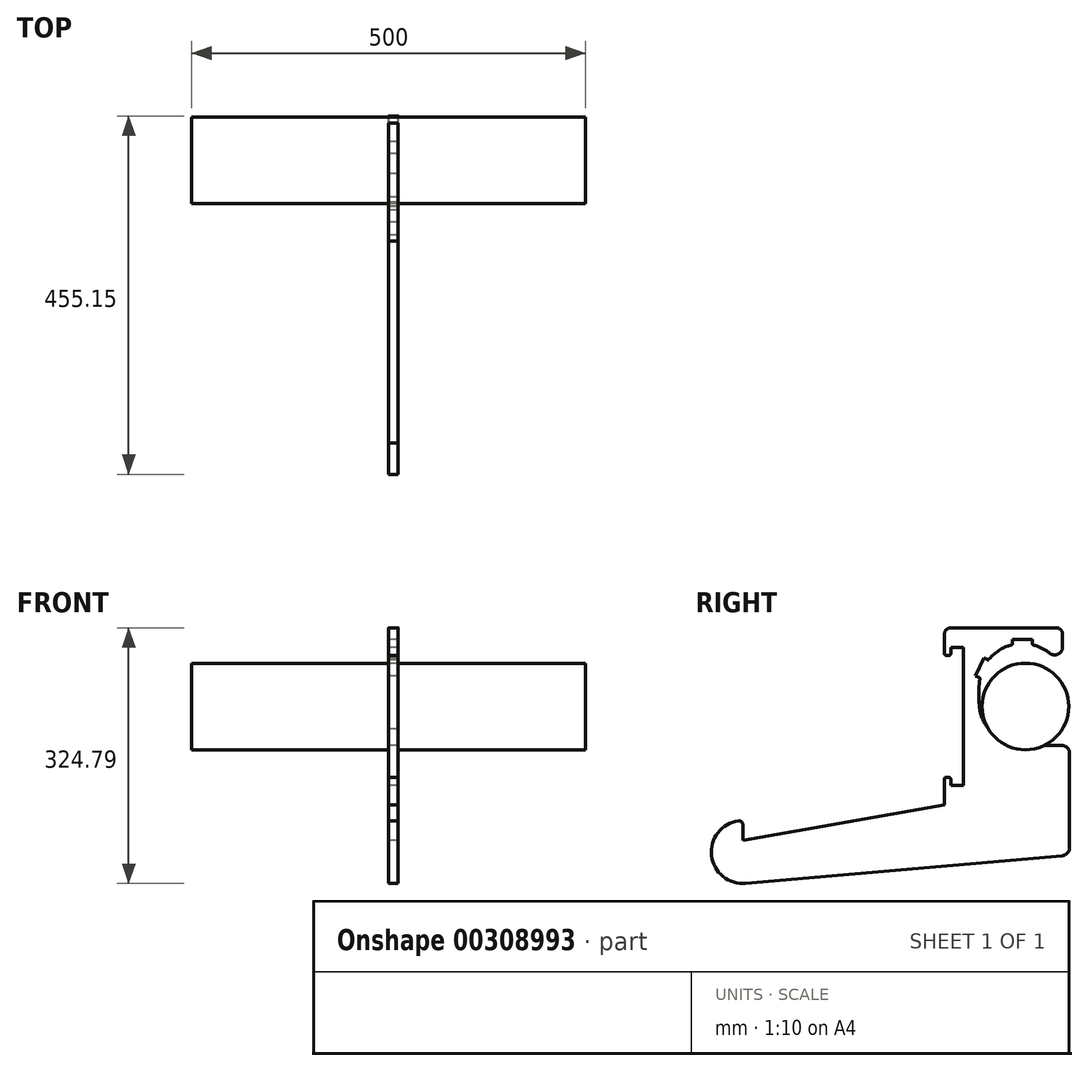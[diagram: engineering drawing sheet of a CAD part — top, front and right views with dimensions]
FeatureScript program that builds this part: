
annotation { "Feature Type Name" : "Feature", "Feature Type Description" : "" }
export const myFeature = defineFeature(function(context is Context, id is Id, definition is map)
    precondition{}
    {
        {
            var Q0;
            Q0=qCreatedBy(makeId("Right.planeOp"),FACE);
            var sketch = newSketch(context, id + "F0", { "sketchPlane" : qUnion([Q0])});
            skCircle(sketch, "E0", {"center": v(-60, 100) * mm, "radius": 55 * mm});
            skSolve(sketch);
        }
        {
            var Q0;
            Q0=makeQuery(id+"F0.imprint","IMPRINT",FACE,{"disambiguationData":[TD([[makeQuery(id+"F0.imprint","IMPRINT",EDGE,{"derivedFrom":sQuery(id+"F0.wireOp",EDGE,"E0")}),1.0]])]});
            extrude(context, id + "F1", {"entities" : qUnion([Q0]), "depth" : 250 * mm, "hasSecondDirection" : true, "secondDirectionOppositeDirection" : true, "secondDirectionDepth" : 250 * mm});
        }
        {
            var Q0;
            Q0=qCreatedBy(makeId("Right.planeOp"),FACE);
            var sketch = newSketch(context, id + "F2", { "sketchPlane" : qUnion([Q0])});
            skLineSegment(sketch, "E1", {"start": v(-12.91, 175.52) * mm, "end": v(-12.91, 200) * mm});
            skLineSegment(sketch, "E2", {"start": v(-12.91, 200) * mm, "end": v(-162.91, 200) * mm});
            skLineSegment(sketch, "E3", {"start": v(-162.91, 200) * mm, "end": v(-162.91, 165) * mm});
            skLineSegment(sketch, "E4", {"start": v(-162.91, -25) * mm, "end": v(-418.96, -70.15) * mm});
            skLineSegment(sketch, "E5", {"start": v(-118.81, 105.52) * mm, "end": v(-118.81, 125) * mm});
            skArc(sketch, "E6", {"start": v(-29.2, 167.75) * mm, "mid": v(-39.65, 174.4) * mm, "end": v(-51.31, 178.56) * mm});
            skLineSegment(sketch, "E7.top", {"start": v(-76.31, 185) * mm, "end": v(-51.31, 185) * mm});
            skLineSegment(sketch, "E7.left", {"start": v(-76.31, 178.56) * mm, "end": v(-76.31, 185) * mm});
            skLineSegment(sketch, "E7.right", {"start": v(-51.31, 178.56) * mm, "end": v(-51.31, 185) * mm});
            skLineSegment(sketch, "E8", {"start": v(-107.07, 158.96) * mm, "end": v(-112.9, 161.69) * mm});
            skLineSegment(sketch, "E9", {"start": v(-112.9, 161.69) * mm, "end": v(-123.47, 139.03) * mm});
            skLineSegment(sketch, "E10", {"start": v(-123.47, 139.03) * mm, "end": v(-117.64, 136.3) * mm});
            skPoint(sketch, "E11", {"position": v(-63.81, 185) * mm});
            skArc(sketch, "E12.trimOffspring", {"start": v(-76.31, 178.56) * mm, "mid": v(-93.36, 171.39) * mm, "end": v(-107.07, 158.96) * mm});
            skLineSegment(sketch, "E13", {"start": v(-63.81, 125) * mm, "end": v(-118.2, 150.36) * mm, "construction": true});
            skArc(sketch, "E14.trimOffspring", {"start": v(-117.64, 136.3) * mm, "mid": v(-118.52, 130.68) * mm, "end": v(-118.81, 125) * mm});
            skLineSegment(sketch, "E15", {"start": v(-3.81, -79.46) * mm, "end": v(-3.81, 40.52) * mm});
            skLineSegment(sketch, "E16", {"start": v(-13.81, 50.52) * mm, "end": v(-63.81, 50.52) * mm});
            skArc(sketch, "E17.filletArc", {"start": v(-29.2, 167.75) * mm, "mid": v(-18.6, 166.5) * mm, "end": v(-12.91, 175.52) * mm});
            skPoint(sketch, "E18", {"position": v(-22.91, 165.52) * mm});
            skArc(sketch, "E19.filletArc", {"start": v(-118.81, 105.52) * mm, "mid": v(-102.7, 66.63) * mm, "end": v(-63.81, 50.52) * mm});
            skArc(sketch, "E20.filletArc", {"start": v(-3.81, 40.52) * mm, "mid": v(-6.74, 47.6) * mm, "end": v(-13.81, 50.52) * mm});
            skPoint(sketch, "E21.visualSharp", {"position": v(-3.81, -50) * mm});
            skArc(sketch, "E21.filletArc", {"start": v(-12.94, -89.42) * mm, "mid": v(-6.44, -86.21) * mm, "end": v(-3.81, -79.46) * mm});
            skLineSegment(sketch, "E22.top", {"start": v(-154.91, 175) * mm, "end": v(-138.81, 175) * mm});
            skLineSegment(sketch, "E22.right", {"start": v(-138.81, 0) * mm, "end": v(-138.81, 175) * mm});
            skLineSegment(sketch, "E23", {"start": v(-162.91, 165) * mm, "end": v(-154.91, 165) * mm});
            skLineSegment(sketch, "E24.trimOffspring", {"start": v(-162.91, 10) * mm, "end": v(-162.91, -25) * mm});
            skLineSegment(sketch, "E25.trimOffspring", {"start": v(-154.91, 165) * mm, "end": v(-154.91, 175) * mm});
            skLineSegment(sketch, "E26", {"start": v(-138.81, 0) * mm, "end": v(-154.91, 0) * mm});
            skLineSegment(sketch, "E27", {"start": v(-154.91, 0) * mm, "end": v(-154.91, 10) * mm});
            skLineSegment(sketch, "E28", {"start": v(-154.91, 10) * mm, "end": v(-162.91, 10) * mm});
            skLineSegment(sketch, "E29", {"start": v(-418.96, -70.15) * mm, "end": v(-418.96, -50.15) * mm});
            skArc(sketch, "E30", {"start": v(-424.68, -45.2) * mm, "mid": v(-458.7, -89.4) * mm, "end": v(-415.48, -124.64) * mm});
            skLineSegment(sketch, "E31", {"start": v(-12.94, -89.42) * mm, "end": v(-415.48, -124.64) * mm});
            skPoint(sketch, "E32.visualSharp", {"position": v(-418.96, -44.79) * mm});
            skArc(sketch, "E32.filletArc", {"start": v(-418.96, -50.15) * mm, "mid": v(-420.7, -46.37) * mm, "end": v(-424.68, -45.2) * mm});
            skSolve(sketch);
        }
        {
            var Q0;
            Q0=makeQuery(id+"F2.imprint","IMPRINT",FACE,{"disambiguationData":[TD([[makeQuery(id+"F2.imprint","IMPRINT",EDGE,{"derivedFrom":sQuery(id+"F2.wireOp",EDGE,"E1")}),1.0]])]});
            extrude(context, id + "F3", {"entities" : qUnion([Q0]), "operationType" : NewBodyOperationType.ADD, "depth" : 12 * mm});
        }
        {
            var Q0;
            Q0=makeQuery(id+"F3.opExtrude","SWEPT_EDGE",EDGE,{"disambiguationData":[OSD([sQuery(id+"F2.wireOp",EDGE,"E2"),sQuery(id+"F2.wireOp",EDGE,"E3")])]});
            var Q1;
            Q1=makeQuery(id+"F3.opExtrude","SWEPT_EDGE",EDGE,{"disambiguationData":[OSD([sQuery(id+"F2.wireOp",EDGE,"E1"),sQuery(id+"F2.wireOp",EDGE,"E2")])]});
            fillet(context, id + "F4", {"entities" : qUnion([Q0, Q1]), "radius" : 8 * mm, "tangentPropagation" : true, "allowEdgeOverflow" : false});
        }
        {
            var Q0;
            Q0=makeQuery(id+"F3.opExtrude","SWEPT_EDGE",EDGE,{"disambiguationData":[OSD([sQuery(id+"F2.wireOp",EDGE,"E3"),sQuery(id+"F2.wireOp",EDGE,"E23")])]});
            var Q1;
            Q1=makeQuery(id+"F3.opExtrude","SWEPT_EDGE",EDGE,{"disambiguationData":[OSD([sQuery(id+"F2.wireOp",EDGE,"E24.trimOffspring"),sQuery(id+"F2.wireOp",EDGE,"E28")])]});
            var Q2;
            Q2=makeQuery(id+"F3.opExtrude","SWEPT_EDGE",EDGE,{"disambiguationData":[OSD([sQuery(id+"F2.wireOp",EDGE,"E23"),sQuery(id+"F2.wireOp",EDGE,"E25.trimOffspring")])]});
            var Q3;
            Q3=makeQuery(id+"F3.opExtrude","SWEPT_EDGE",EDGE,{"disambiguationData":[OSD([sQuery(id+"F2.wireOp",EDGE,"E8"),sQuery(id+"F2.wireOp",EDGE,"E12.trimOffspring")])]});
            var Q4;
            Q4=makeQuery(id+"F3.opExtrude","SWEPT_EDGE",EDGE,{"disambiguationData":[OSD([sQuery(id+"F2.wireOp",EDGE,"E10"),sQuery(id+"F2.wireOp",EDGE,"E14.trimOffspring")])]});
            var Q5;
            Q5=makeQuery(id+"F3.opExtrude","SWEPT_EDGE",EDGE,{"disambiguationData":[OSD([sQuery(id+"F2.wireOp",EDGE,"E7.left"),sQuery(id+"F2.wireOp",EDGE,"E12.trimOffspring")])]});
            var Q6;
            Q6=makeQuery(id+"F3.opExtrude","SWEPT_EDGE",EDGE,{"disambiguationData":[OSD([sQuery(id+"F2.wireOp",EDGE,"E6"),sQuery(id+"F2.wireOp",EDGE,"E7.right")])]});
            var Q7;
            Q7=makeQuery(id+"F3.opExtrude","SWEPT_EDGE",EDGE,{"disambiguationData":[OSD([sQuery(id+"F2.wireOp",EDGE,"E27"),sQuery(id+"F2.wireOp",EDGE,"E28")])]});
            fillet(context, id + "F5", {"entities" : qUnion([Q0, Q1, Q2, Q3, Q4, Q5, Q6, Q7]), "radius" : 2 * mm, "tangentPropagation" : true, "allowEdgeOverflow" : false});
        }
    });
